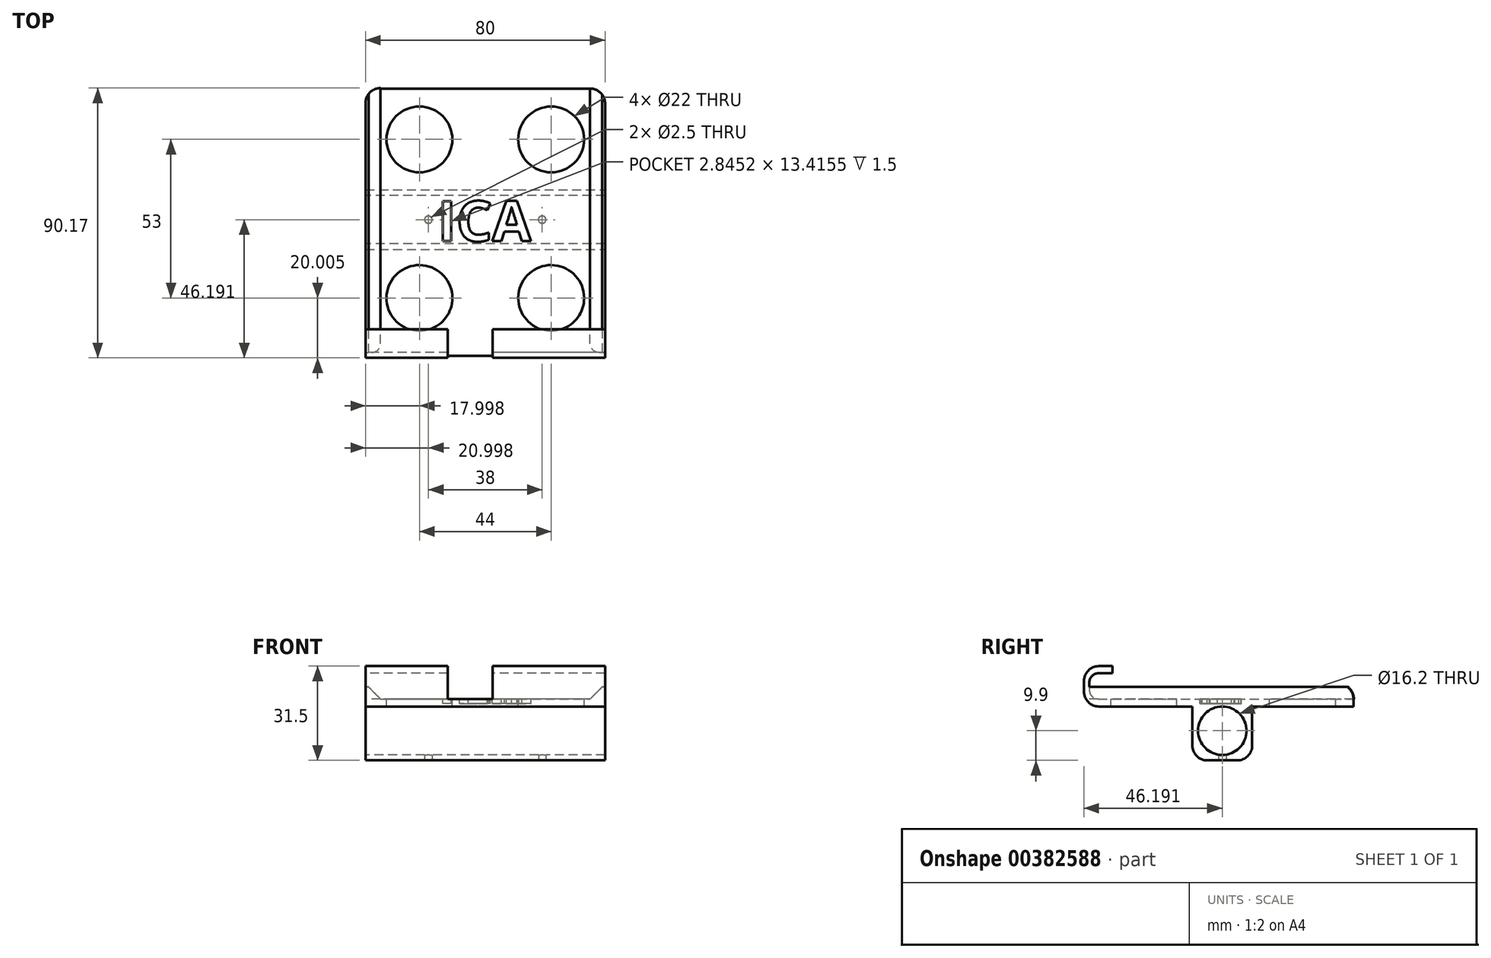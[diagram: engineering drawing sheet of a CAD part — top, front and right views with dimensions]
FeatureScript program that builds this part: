
annotation { "Feature Type Name" : "Feature", "Feature Type Description" : "" }
export const myFeature = defineFeature(function(context is Context, id is Id, definition is map)
    precondition{}
    {
        {
            var Q0;
            Q0=qCreatedBy(makeId("Top.planeOp"),FACE);
            var sketch = newSketch(context, id + "F0", { "sketchPlane" : qUnion([Q0])});
            skLineSegment(sketch, "E0.bottom", {"start": v(-32.63, 35.2) * mm, "end": v(47.37, 35.2) * mm});
            skLineSegment(sketch, "E0.top", {"start": v(-32.63, -54.8) * mm, "end": v(47.37, -54.8) * mm});
            skLineSegment(sketch, "E0.left", {"start": v(-32.63, 35.2) * mm, "end": v(-32.63, -54.8) * mm});
            skLineSegment(sketch, "E0.right", {"start": v(47.37, 35.2) * mm, "end": v(47.37, -54.8) * mm});
            skSolve(sketch);
        }
        {
            var Q0;
            Q0=qSketchRegion(id+"F0",true);
            extrude(context, id + "F1", {"entities" : qUnion([Q0]), "depth" : 2.5 * mm});
        }
        {
            var Q0;
            Q0=makeQuery(id+"F1.opExtrude","CAP_FACE",FACE,{"disambiguationData":[OSD([sQuery(id+"F0.wireOp",EDGE,"E0.bottom"),sQuery(id+"F0.wireOp",EDGE,"E0.top"),sQuery(id+"F0.wireOp",EDGE,"E0.left"),sQuery(id+"F0.wireOp",EDGE,"E0.right")])],"isStart":false});
            var sketch = newSketch(context, id + "F2", { "sketchPlane" : qUnion([Q0])});
            skLineSegment(sketch, "E1.bottom", {"start": v(-32.63, -45.3) * mm, "end": v(47.37, -45.3) * mm});
            skLineSegment(sketch, "E1.top", {"start": v(-32.63, -54.8) * mm, "end": v(47.37, -54.8) * mm});
            skLineSegment(sketch, "E1.left", {"start": v(-32.63, -45.3) * mm, "end": v(-32.63, -54.8) * mm});
            skLineSegment(sketch, "E1.right", {"start": v(47.37, -45.3) * mm, "end": v(47.37, -54.8) * mm});
            skSolve(sketch);
        }
        {
            var Q0;
            Q0=qSketchRegion(id+"F2",true);
            extrude(context, id + "F3", {"entities" : qUnion([Q0]), "operationType" : NewBodyOperationType.ADD, "depth" : 11 * mm});
        }
        {
            var Q0;
            Q0=makeQuery(id+"F3.boolean.opBoolean","MERGE",FACE,{"derivedFrom":[makeQuery(id+"F1.opExtrude","SWEPT_FACE",FACE,{"disambiguationData":[OSD([sQuery(id+"F0.wireOp",EDGE,"E0.left")])]}),makeQuery(id+"F3.opExtrude","SWEPT_FACE",FACE,{"disambiguationData":[OSD([sQuery(id+"F2.wireOp",EDGE,"E1.left")])]})]});
            var sketch = newSketch(context, id + "F4", { "sketchPlane" : qUnion([Q0])});
            skLineSegment(sketch, "E2.bottom", {"start": v(45.3, 11.09) * mm, "end": v(53, 11.09) * mm});
            skLineSegment(sketch, "E2.top", {"start": v(45.3, 2.5) * mm, "end": v(53, 2.5) * mm});
            skLineSegment(sketch, "E2.left", {"start": v(45.3, 11.09) * mm, "end": v(45.3, 2.5) * mm});
            skLineSegment(sketch, "E2.right", {"start": v(53, 11.09) * mm, "end": v(53, 2.5) * mm});
            skSolve(sketch);
        }
        {
            var Q0;
            Q0=qSketchRegion(id+"F4",true);
            extrude(context, id + "F5", {"entities" : qUnion([Q0]), "operationType" : NewBodyOperationType.REMOVE, "oppositeDirection" : true, "depth" : 90 * mm});
        }
        {
            var Q0;
            Q0=makeQuery(id+"F3.opExtrude","CAP_EDGE",EDGE,{"disambiguationData":[OSD([sQuery(id+"F2.wireOp",EDGE,"E1.top")])],"isStart":false});
            var Q1;
            Q1=makeQuery(id+"F1.opExtrude","CAP_EDGE",EDGE,{"disambiguationData":[OSD([sQuery(id+"F0.wireOp",EDGE,"E0.top")])],"isStart":true});
            fillet(context, id + "F6", {"entities" : qUnion([Q0, Q1]), "radius" : 5 * mm, "tangentPropagation" : true, "allowEdgeOverflow" : false});
        }
        {
            var Q0;
            Q0=makeQuery(id+"F1.opExtrude","CAP_FACE",FACE,{"disambiguationData":[OSD([sQuery(id+"F0.wireOp",EDGE,"E0.bottom"),sQuery(id+"F0.wireOp",EDGE,"E0.top"),sQuery(id+"F0.wireOp",EDGE,"E0.left"),sQuery(id+"F0.wireOp",EDGE,"E0.right")])],"isStart":true});
            var sketch = newSketch(context, id + "F7", { "sketchPlane" : qUnion([Q0])});
            skLineSegment(sketch, "E3.bottom", {"start": v(-32.63, 18.62) * mm, "end": v(47.37, 18.62) * mm});
            skLineSegment(sketch, "E3.top", {"start": v(-32.63, -1.38) * mm, "end": v(47.37, -1.38) * mm});
            skLineSegment(sketch, "E3.left", {"start": v(-32.63, 18.62) * mm, "end": v(-32.63, -1.38) * mm});
            skLineSegment(sketch, "E3.right", {"start": v(47.37, 18.62) * mm, "end": v(47.37, -1.38) * mm});
            skSolve(sketch);
        }
        {
            var Q0;
            Q0=qSketchRegion(id+"F7",true);
            extrude(context, id + "F8", {"entities" : qUnion([Q0]), "operationType" : NewBodyOperationType.ADD, "depth" : 18 * mm});
        }
        {
            var Q0;
            Q0=makeQuery(id+"F8.boolean.opBoolean","MERGE",FACE,{"derivedFrom":[makeQuery(id+"F3.boolean.opBoolean","MERGE",FACE,{"derivedFrom":[makeQuery(id+"F1.opExtrude","SWEPT_FACE",FACE,{"disambiguationData":[OSD([sQuery(id+"F0.wireOp",EDGE,"E0.left")])]}),makeQuery(id+"F3.opExtrude","SWEPT_FACE",FACE,{"disambiguationData":[OSD([sQuery(id+"F2.wireOp",EDGE,"E1.left")])]})]}),makeQuery(id+"F8.opExtrude","SWEPT_FACE",FACE,{"disambiguationData":[OSD([sQuery(id+"F7.wireOp",EDGE,"E3.left")])]})]});
            var sketch = newSketch(context, id + "F9", { "sketchPlane" : qUnion([Q0])});
            skCircle(sketch, "E4", {"center": v(8.62, -8.1) * mm, "radius": 8.1 * mm});
            skSolve(sketch);
        }
        {
            var Q0;
            Q0=qSketchRegion(id+"F9",true);
            extrude(context, id + "F10", {"entities" : qUnion([Q0]), "operationType" : NewBodyOperationType.REMOVE, "oppositeDirection" : true, "depth" : 90 * mm});
        }
        {
            var Q0;
            Q0=makeQuery(id+"F8.opExtrude","CAP_EDGE",EDGE,{"disambiguationData":[OSD([sQuery(id+"F7.wireOp",EDGE,"E3.bottom")])],"isStart":false});
            var Q1;
            Q1=makeQuery(id+"F8.opExtrude","CAP_EDGE",EDGE,{"disambiguationData":[OSD([sQuery(id+"F7.wireOp",EDGE,"E3.top")])],"isStart":false});
            var Q2;
            Q2=makeQuery(id+"F1.opExtrude","SWEPT_EDGE",EDGE,{"disambiguationData":[OSD([sQuery(id+"F0.wireOp",EDGE,"E0.bottom"),sQuery(id+"F0.wireOp",EDGE,"E0.right")])]});
            var Q3;
            Q3=makeQuery(id+"F1.opExtrude","SWEPT_EDGE",EDGE,{"disambiguationData":[OSD([sQuery(id+"F0.wireOp",EDGE,"E0.bottom"),sQuery(id+"F0.wireOp",EDGE,"E0.left")])]});
            fillet(context, id + "F11", {"entities" : qUnion([Q0, Q1, Q2, Q3]), "radius" : 5 * mm, "tangentPropagation" : true, "allowEdgeOverflow" : false});
        }
        {
            var Q0;
            Q0=makeQuery(id+"F5.boolean.opBoolean","COPY",EDGE,{"derivedFrom":makeQuery(id+"F5.opExtrude","SWEPT_EDGE",EDGE,{"disambiguationData":[OSD([sQuery(id+"F4.wireOp",EDGE,"E2.bottom"),sQuery(id+"F4.wireOp",EDGE,"E2.right")])]})});
            var Q1;
            Q1=makeQuery(id+"F5.boolean.opBoolean","COPY",EDGE,{"derivedFrom":makeQuery(id+"F5.opExtrude","SWEPT_EDGE",EDGE,{"disambiguationData":[OSD([sQuery(id+"F4.wireOp",EDGE,"E2.top"),sQuery(id+"F4.wireOp",EDGE,"E2.right")])]})});
            fillet(context, id + "F12", {"entities" : qUnion([Q0, Q1]), "radius" : 3 * mm, "tangentPropagation" : true, "allowEdgeOverflow" : false});
        }
        {
            var Q0;
            Q0=makeQuery(id+"F8.opExtrude","CAP_FACE",FACE,{"disambiguationData":[OSD([sQuery(id+"F7.wireOp",EDGE,"E3.bottom"),sQuery(id+"F7.wireOp",EDGE,"E3.top"),sQuery(id+"F7.wireOp",EDGE,"E3.left"),sQuery(id+"F7.wireOp",EDGE,"E3.right")])],"isStart":false});
            var sketch = newSketch(context, id + "F13", { "sketchPlane" : qUnion([Q0])});
            skCircle(sketch, "E5", {"center": v(-11.63, 8.62) * mm, "radius": 1.25 * mm});
            skPoint(sketch, "E5.centerSnap0", {"position": v(-32.63, 8.62) * mm});
            skCircle(sketch, "E6", {"center": v(26.37, 8.62) * mm, "radius": 1.25 * mm});
            skSolve(sketch);
        }
        {
            var Q0;
            Q0=qSketchRegion(id+"F13",true);
            extrude(context, id + "F14", {"entities" : qUnion([Q0]), "operationType" : NewBodyOperationType.REMOVE, "oppositeDirection" : true, "depth" : 5 * mm});
        }
        {
            var Q0;
            Q0=makeQuery(id+"F5.boolean.opBoolean","MERGE",FACE,{"derivedFrom":[makeQuery(id+"F1.opExtrude","CAP_FACE",FACE,{"disambiguationData":[OSD([sQuery(id+"F0.wireOp",EDGE,"E0.bottom"),sQuery(id+"F0.wireOp",EDGE,"E0.top"),sQuery(id+"F0.wireOp",EDGE,"E0.left"),sQuery(id+"F0.wireOp",EDGE,"E0.right")])],"isStart":false}),makeQuery(id+"F5.opExtrude","SWEPT_FACE",FACE,{"disambiguationData":[OSD([sQuery(id+"F4.wireOp",EDGE,"E2.top")])]})]});
            var sketch = newSketch(context, id + "F15", { "sketchPlane" : qUnion([Q0])});
            skCircle(sketch, "E7", {"center": v(-14.63, 18.2) * mm, "radius": 11 * mm});
            skCircle(sketch, "E8", {"center": v(29.37, 18.2) * mm, "radius": 11 * mm});
            skCircle(sketch, "E9", {"center": v(-14.63, -34.8) * mm, "radius": 11 * mm});
            skCircle(sketch, "E10", {"center": v(29.37, -34.8) * mm, "radius": 11 * mm});
            skSolve(sketch);
        }
        {
            var Q0;
            Q0=qSketchRegion(id+"F15",true);
            extrude(context, id + "F16", {"entities" : qUnion([Q0]), "operationType" : NewBodyOperationType.REMOVE, "oppositeDirection" : true, "depth" : 25 * mm});
        }
        {
            var Q0;
            Q0=makeQuery(id+"F5.boolean.opBoolean","MERGE",FACE,{"derivedFrom":[makeQuery(id+"F1.opExtrude","CAP_FACE",FACE,{"disambiguationData":[OSD([sQuery(id+"F0.wireOp",EDGE,"E0.bottom"),sQuery(id+"F0.wireOp",EDGE,"E0.top"),sQuery(id+"F0.wireOp",EDGE,"E0.left"),sQuery(id+"F0.wireOp",EDGE,"E0.right")])],"isStart":false}),makeQuery(id+"F5.opExtrude","SWEPT_FACE",FACE,{"disambiguationData":[OSD([sQuery(id+"F4.wireOp",EDGE,"E2.top")])]})]});
            var sketch = newSketch(context, id + "F17", { "sketchPlane" : qUnion([Q0])});
            skText(sketch, "E11", { "text": "ICA", "fontName": "OpenSans-Bold.ttf"});
            const initialGuessF17  = {"E11": [-0.00854, -0.01584, 1, 0, 0.01353]};
            skSetInitialGuess(sketch, initialGuessF17);
            skSolve(sketch);
        }
        {
            var Q0;
            Q0=qSketchRegion(id+"F17",true);
            extrude(context, id + "F18", {"entities" : qUnion([Q0]), "operationType" : NewBodyOperationType.REMOVE, "oppositeDirection" : true, "depth" : 1.5 * mm});
        }
        {
            var Q0;
            {var subQ0=sQuery(id+"F0.wireOp",EDGE,"E0.right");var subQ1=sQuery(id+"F0.wireOp",EDGE,"E0.left");var subQ2=sQuery(id+"F0.wireOp",EDGE,"E0.bottom");var subQ3=sQuery(id+"F4.wireOp",EDGE,"E2.top");Q0=makeQuery(id+"F18.boolean.opBoolean","SPLIT",FACE,{"disambiguationData":[TD([makeQuery(id+"F1.opExtrude","SWEPT_FACE",FACE,{"disambiguationData":[OSD([subQ2])]})])],"derivedFrom":makeQuery(id+"F5.boolean.opBoolean","MERGE",FACE,{"derivedFrom":[makeQuery(id+"F1.opExtrude","CAP_FACE",FACE,{"disambiguationData":[OSD([subQ2,sQuery(id+"F0.wireOp",EDGE,"E0.top"),subQ1,subQ0])],"isStart":false}),makeQuery(id+"F5.opExtrude","SWEPT_FACE",FACE,{"disambiguationData":[OSD([subQ3])]})]})});}
            var sketch = newSketch(context, id + "F19", { "sketchPlane" : qUnion([Q0])});
            skPoint(sketch, "E12.firstSnap0", {"position": v(-27.63, 17.95) * mm});
            skPoint(sketch, "E12.oppositeSnap0", {"position": v(-32.63, -9.9) * mm});
            skLineSegment(sketch, "E12.bottom", {"start": v(-27.63, -53.84) * mm, "end": v(-32.63, -53.84) * mm});
            skLineSegment(sketch, "E12.top", {"start": v(-27.63, 35.36) * mm, "end": v(-32.63, 35.36) * mm});
            skLineSegment(sketch, "E12.left", {"start": v(-27.63, -53.84) * mm, "end": v(-27.63, 35.36) * mm});
            skLineSegment(sketch, "E12.right", {"start": v(-32.63, -53.84) * mm, "end": v(-32.63, 35.36) * mm});
            skLineSegment(sketch, "E13.bottom", {"start": v(47.37, -54.12) * mm, "end": v(42.37, -54.12) * mm});
            skLineSegment(sketch, "E13.top", {"start": v(47.37, 35.2) * mm, "end": v(42.37, 35.2) * mm});
            skLineSegment(sketch, "E13.left", {"start": v(47.37, -54.12) * mm, "end": v(47.37, 35.2) * mm});
            skLineSegment(sketch, "E13.right", {"start": v(42.37, -54.12) * mm, "end": v(42.37, 35.2) * mm});
            skSolve(sketch);
        }
        {
            var Q0;
            Q0=qSketchRegion(id+"F19",true);
            extrude(context, id + "F20", {"entities" : qUnion([Q0]), "operationType" : NewBodyOperationType.ADD, "depth" : 4 * mm});
        }
        {
            var Q0;
            Q0=makeQuery(id+"F20.opExtrude","SWEPT_EDGE",EDGE,{"disambiguationData":[OSD([sQuery(id+"F19.wireOp",EDGE,"E12.top"),sQuery(id+"F19.wireOp",EDGE,"E12.right")])]});
            var Q1;
            Q1=makeQuery(id+"F20.opExtrude","SWEPT_EDGE",EDGE,{"disambiguationData":[OSD([sQuery(id+"F19.wireOp",EDGE,"E13.top"),sQuery(id+"F19.wireOp",EDGE,"E13.left")])]});
            fillet(context, id + "F21", {"entities" : qUnion([Q0, Q1]), "radius" : 5 * mm, "tangentPropagation" : true, "allowEdgeOverflow" : false});
        }
        {
            var Q0;
            Q0=makeQuery(id+"F20.opExtrude","CAP_EDGE",EDGE,{"disambiguationData":[OSD([sQuery(id+"F19.wireOp",EDGE,"E12.left")])],"isStart":false});
            var Q1;
            Q1=makeQuery(id+"F20.opExtrude","CAP_EDGE",EDGE,{"disambiguationData":[OSD([sQuery(id+"F19.wireOp",EDGE,"E13.right")])],"isStart":false});
            chamfer(context, id + "F22", {"entities" : qUnion([Q0, Q1]), "width" : 4 * mm, "tangentPropagation" : true});
        }
        {
            var Q0;
            {var subQ9=sQuery(id+"F4.wireOp",EDGE,"E2.top");var subQ14=makeQuery(id+"F16.boolean.opBoolean","COPY",FACE,{"derivedFrom":makeQuery(id+"F16.opExtrude","SWEPT_FACE",FACE,{"disambiguationData":[OSD([sQuery(id+"F15.wireOp",EDGE,"yZauCf2Q-no7u-zMMO-hUYj-Ajbo3V0nzf9A.bottom")])]})});var subQ36=sQuery(id+"F0.wireOp",EDGE,"E0.right");var subQ37=sQuery(id+"F0.wireOp",EDGE,"E0.left");var subQ38=sQuery(id+"F0.wireOp",EDGE,"E0.bottom");Q0=makeQuery(id+"F20.boolean.opBoolean","SPLIT",FACE,{"disambiguationData":[TD([subQ14])],"derivedFrom":makeQuery(id+"F18.boolean.opBoolean","SPLIT",FACE,{"disambiguationData":[TD([makeQuery(id+"F1.opExtrude","SWEPT_FACE",FACE,{"disambiguationData":[OSD([subQ38])]})])],"derivedFrom":makeQuery(id+"F5.boolean.opBoolean","MERGE",FACE,{"derivedFrom":[makeQuery(id+"F1.opExtrude","CAP_FACE",FACE,{"disambiguationData":[OSD([subQ38,sQuery(id+"F0.wireOp",EDGE,"E0.top"),subQ37,subQ36])],"isStart":false}),makeQuery(id+"F5.opExtrude","SWEPT_FACE",FACE,{"disambiguationData":[OSD([subQ9])]})]})})});}
            var sketch = newSketch(context, id + "F23", { "sketchPlane" : qUnion([Q0])});
            skLineSegment(sketch, "E14.bottom", {"start": v(-5.13, -40.82) * mm, "end": v(9.87, -40.82) * mm});
            skLineSegment(sketch, "E14.top", {"start": v(-5.13, -59.46) * mm, "end": v(9.87, -59.46) * mm});
            skLineSegment(sketch, "E14.left", {"start": v(-5.13, -40.82) * mm, "end": v(-5.13, -59.46) * mm});
            skLineSegment(sketch, "E14.right", {"start": v(9.87, -40.82) * mm, "end": v(9.87, -59.46) * mm});
            skSolve(sketch);
        }
        {
            var Q0;
            Q0=qSketchRegion(id+"F23",true);
            extrude(context, id + "F24", {"entities" : qUnion([Q0]), "operationType" : NewBodyOperationType.REMOVE, "depth" : 25 * mm});
        }
    });
